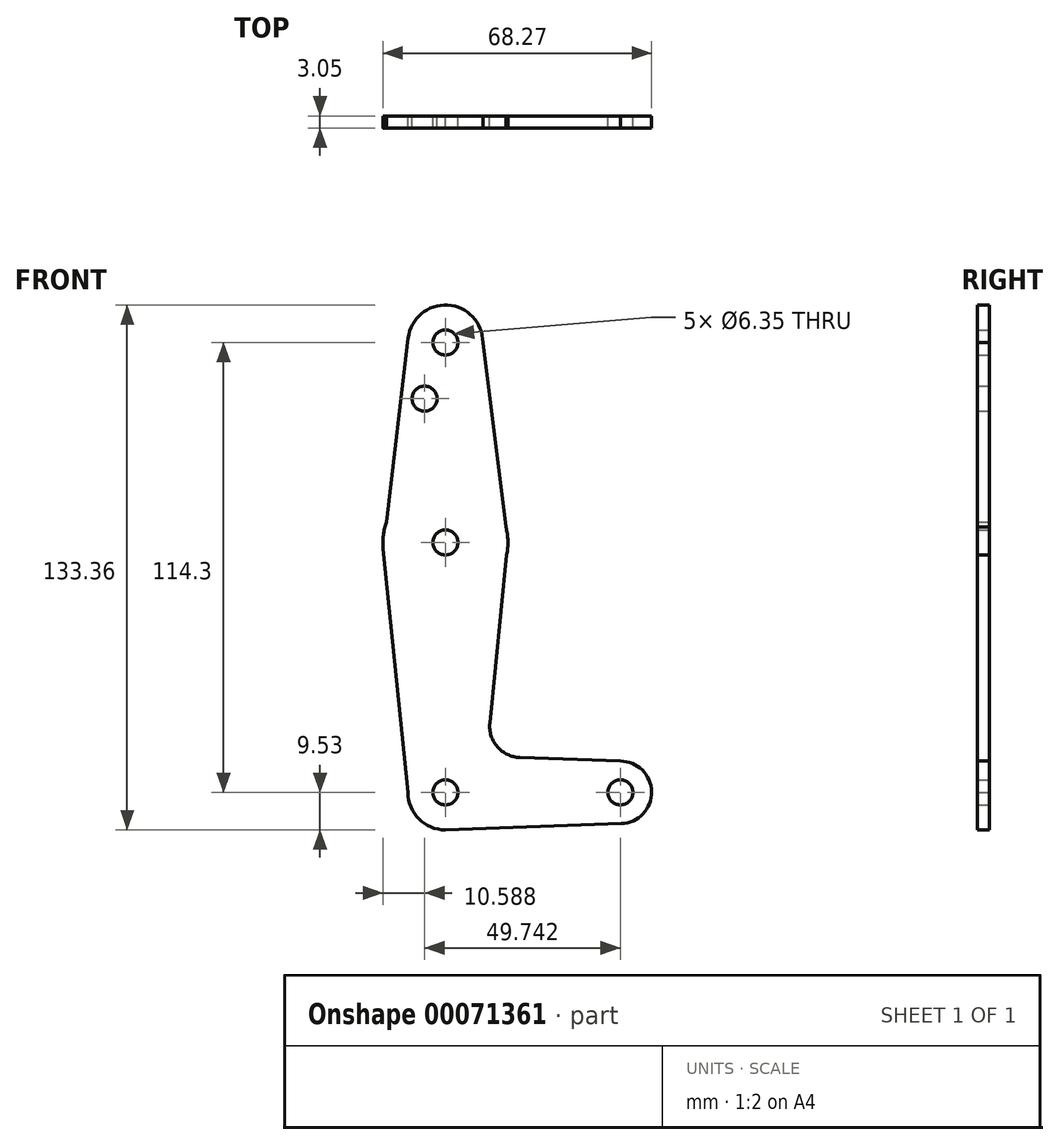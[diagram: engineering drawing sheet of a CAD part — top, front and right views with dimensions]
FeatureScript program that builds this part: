
annotation { "Feature Type Name" : "Feature", "Feature Type Description" : "" }
export const myFeature = defineFeature(function(context is Context, id is Id, definition is map)
    precondition{}
    {
        {
            var Q0;
            Q0=qCreatedBy(makeId("Front.planeOp"),FACE);
            var sketch = newSketch(context, id + "F0", { "sketchPlane" : qUnion([Q0])});
            skLineSegment(sketch, "E0", {"start": v(0, 114.3) * mm, "end": v(0, 0) * mm, "construction": true});
            skLineSegment(sketch, "E1", {"start": v(0, 0) * mm, "end": v(44.45, 0) * mm, "construction": true});
            skCircle(sketch, "E2", {"center": v(0, 114.3) * mm, "radius": 9.53 * mm});
            skCircle(sketch, "E3", {"center": v(0, 63.5) * mm, "radius": 15.88 * mm});
            skCircle(sketch, "E4", {"center": v(0, 0) * mm, "radius": 9.53 * mm});
            skCircle(sketch, "E5", {"center": v(44.45, 0) * mm, "radius": 7.94 * mm});
            skLineSegment(sketch, "E6", {"start": v(-9.53, 0) * mm, "end": v(-15.8, 61.9) * mm});
            skLineSegment(sketch, "E7", {"start": v(-15.8, 61.9) * mm, "end": v(-9.46, 115.42) * mm});
            skLineSegment(sketch, "E8", {"start": v(11.28, 17.59) * mm, "end": v(15.88, 63.5) * mm});
            skLineSegment(sketch, "E9", {"start": v(15.88, 63.5) * mm, "end": v(9.53, 114.3) * mm});
            skLineSegment(sketch, "E10", {"start": v(0, -9.53) * mm, "end": v(44.73, -7.93) * mm});
            skLineSegment(sketch, "E11", {"start": v(44.45, 7.94) * mm, "end": v(18.9, 8.85) * mm});
            skPoint(sketch, "E12.newPointB", {"position": v(0, 9.53) * mm});
            skArc(sketch, "E12.filletArc", {"start": v(11.28, 17.59) * mm, "mid": v(13.2, 11.57) * mm, "end": v(18.9, 8.85) * mm});
            skCircle(sketch, "E13", {"center": v(0, 63.5) * mm, "radius": 3.18 * mm});
            skCircle(sketch, "E14", {"center": v(0, 0) * mm, "radius": 3.18 * mm});
            skCircle(sketch, "E15", {"center": v(44.45, 0) * mm, "radius": 3.18 * mm});
            skCircle(sketch, "E16", {"center": v(0, 114.3) * mm, "radius": 3.18 * mm});
            skCircle(sketch, "E17", {"center": v(-5.3, 100.03) * mm, "radius": 3.18 * mm});
            skSolve(sketch);
        }
        {
            var Q0;
            {var subQ0=sQuery(id+"F0.wireOp",EDGE,"E9");var subQ1=sQuery(id+"F0.wireOp",EDGE,"E3");var subQ3=makeQuery(id+"F0.imprint","INTERSECT",VERTEX,{"derivedFrom":[subQ1,subQ0]});Q0=makeQuery(id+"F0.imprint","IMPRINT",FACE,{"disambiguationData":[TD([[makeQuery(id+"F0.imprint","IMPRINT",EDGE,{"disambiguationData":[TD([[subQ3,1.0]])],"derivedFrom":subQ1}),1.0]])]});}
            var Q1;
            {var subQ0=sQuery(id+"F0.wireOp",EDGE,"E7");var subQ1=sQuery(id+"F0.wireOp",EDGE,"E3");var subQ3=makeQuery(id+"F0.imprint","INTERSECT",VERTEX,{"derivedFrom":[subQ1,subQ0]});Q1=makeQuery(id+"F0.imprint","IMPRINT",FACE,{"disambiguationData":[TD([[makeQuery(id+"F0.imprint","IMPRINT",EDGE,{"disambiguationData":[TD([[subQ3,-1.0]])],"derivedFrom":subQ1}),1.0]])]});}
            var Q2;
            {var subQ0=sQuery(id+"F0.wireOp",EDGE,"E8");var subQ1=sQuery(id+"F0.wireOp",EDGE,"E3");var subQ3=makeQuery(id+"F0.imprint","INTERSECT",VERTEX,{"derivedFrom":[subQ1,subQ0]});Q2=makeQuery(id+"F0.imprint","IMPRINT",FACE,{"disambiguationData":[TD([[makeQuery(id+"F0.imprint","IMPRINT",EDGE,{"disambiguationData":[TD([[subQ3,-1.0]])],"derivedFrom":subQ1}),1.0]])]});}
            var Q3;
            {var subQ0=sQuery(id+"F0.wireOp",EDGE,"E10");var subQ1=sQuery(id+"F0.wireOp",EDGE,"E4");var subQ2=makeQuery(id+"F0.imprint","INTERSECT",VERTEX,{"disambiguationData":[OD(0.0)],"derivedFrom":[subQ1,subQ0]});Q3=makeQuery(id+"F0.imprint","IMPRINT",FACE,{"disambiguationData":[TD([[makeQuery(id+"F0.imprint","IMPRINT",EDGE,{"disambiguationData":[TD([[subQ2,-1.0]])],"derivedFrom":subQ1}),1.0]])]});}
            var Q4;
            Q4=makeQuery(id+"F0.imprint","IMPRINT",FACE,{"disambiguationData":[TD([[makeQuery(id+"F0.imprint","IMPRINT",EDGE,{"derivedFrom":sQuery(id+"F0.wireOp",EDGE,"E16")}),-1.0]])]});
            var Q5;
            Q5=makeQuery(id+"F0.imprint","IMPRINT",FACE,{"disambiguationData":[TD([[makeQuery(id+"F0.imprint","IMPRINT",EDGE,{"derivedFrom":sQuery(id+"F0.wireOp",EDGE,"E15")}),-1.0]])]});
            var Q6;
            Q6=makeQuery(id+"F0.imprint","IMPRINT",FACE,{"disambiguationData":[TD([[makeQuery(id+"F0.imprint","IMPRINT",EDGE,{"derivedFrom":sQuery(id+"F0.wireOp",EDGE,"E17")}),-1.0]])]});
            var Q7;
            {var subQ0=sQuery(id+"F0.wireOp",EDGE,"E6");Q7=makeQuery(id+"F0.imprint","IMPRINT",FACE,{"disambiguationData":[TD([[makeQuery(id+"F0.imprint","IMPRINT",EDGE,{"derivedFrom":subQ0}),-1.0]])]});}
            var Q8;
            Q8=makeQuery(id+"F0.imprint","IMPRINT",FACE,{"disambiguationData":[TD([[makeQuery(id+"F0.imprint","IMPRINT",EDGE,{"derivedFrom":sQuery(id+"F0.wireOp",EDGE,"E14")}),-1.0]])]});
            var Q9;
            Q9=makeQuery(id+"F0.imprint","IMPRINT",FACE,{"disambiguationData":[TD([[makeQuery(id+"F0.imprint","IMPRINT",EDGE,{"derivedFrom":sQuery(id+"F0.wireOp",EDGE,"E13")}),-1.0]])]});
            extrude(context, id + "F1", {"entities" : qUnion([Q0, Q1, Q2, Q3, Q4, Q5, Q6, Q7, Q8, Q9]), "depth" : 3.05 * mm});
        }
    });
